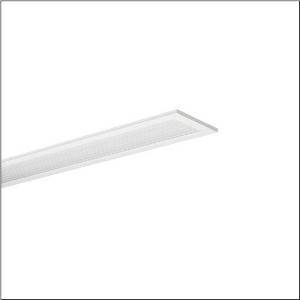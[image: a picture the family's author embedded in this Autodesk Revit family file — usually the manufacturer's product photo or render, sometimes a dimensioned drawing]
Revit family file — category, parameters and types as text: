
# Revit family: apollon_21_linear_51mq15wd2414
name_source: partatom
category: Lighting Fixtures
units: mm (PartAtom-declared; Revit-internal decimal feet)

## family parameters
Cut with Voids When Loaded = No
Host = Face
Light Source = No
Part Type = Normal
Room Calculation Point = No
Round Connector Dimension = Use Diameter
Shared = No

## types (1)
- Apollon 21 linear (1 x LED, 2520 lm, 17.4 W, 4000K)
    Apparent Load = 17 VA
    CIE Flux Codes = 66 89 97 100 100
    Color Rendering = 80
    Color Temperature = 4000K
    Default Elevation = 1800 mm
    Description = Apollon 21 linear, office luminaire, primary optical cover: micro prismatic cover, of PMMA, CAT 2 (L<= 3000cd/m²), light emission: direct distribution, primary light characteristic: symmetric, installation type: lay-in mounting, LED, rated luminous flux: 2.520lm, luminous efficacy: 145lm/W, light colour: 840, colour temperature: 4000K, control gear: DALI 2, Multilumen, with terminal, 5-pole, mains connection: 220..240V, AC/DC, 0/50..60Hz, rated input power: 17.4W, housing, of aluminium, coated, traffic white (RAL 9016), length: 1.245mm, width: 179mm, height: 55mm, recess depth: 180mm, housing upper side, of sheet steel, galvanised, protection rating (complete): IP20, protection rating (lamp compartment, on room side): IP50, insulation class (complete): insulation class II (safety insulation), certification: CE, ENEC, impact resistance: IK03, permissible operating ambient temperature: -20..+45°C, permissible storage temperature: -40..+80°C, standard: EN 60598-2-22, packaging unit: 1 piece
    Height = 0 mm  [stored 0 ft]
    Lamp = 1 x LED
    Lamp Light Flux = 2520 lm
    Lamp Power = 17.4 W
    Lamp count = 1
    Length = 1245 mm
    Luminous efficacy = 145 lm/W
    Manufacturer = Siteco
    ModVariant = No
    Model = 51MQ15WD2414
    Mounting Place = Ceiling
    Mounting Type = Recessed
    Number of Poles = 1
    OnlyDefault = Yes
    Power Factor = 1
    Product Name = Apollon 21 linear
    Product group = office luminaire | ceiling recessed
    ProductGroupID = 401
    Protection Class = Protection class II
    Protection Degree = IP 20
    RLX_Detail_Level = 1
    RLX_Emergency_Light_Flux = 0 lm
    RLX_Emergency_Type = 0
    RLX_Emergency_Type_DB = No
    RlxData = <blob elided: 12601 chars, md5=11ad033d>
    Socket = socket
    Standby Power = 0 W
    System Light Flux = 2520 lm
    System Power = 17 W
    Type Comments = Product without accessories
    Type Image = l_1291018.jpg
    URL = http://relux.com
    VarID = ---
    Voltage = 0 V
    Weight = 0.00 kg
    Width = 179 mm

note: [stored X ft] marks values corroborated as IEEE doubles in the binary element streams (Revit-internal decimal feet)

## geometry (parser evidence)
native form markers: Sweep x10
no freeform markers — native parametric forms only
